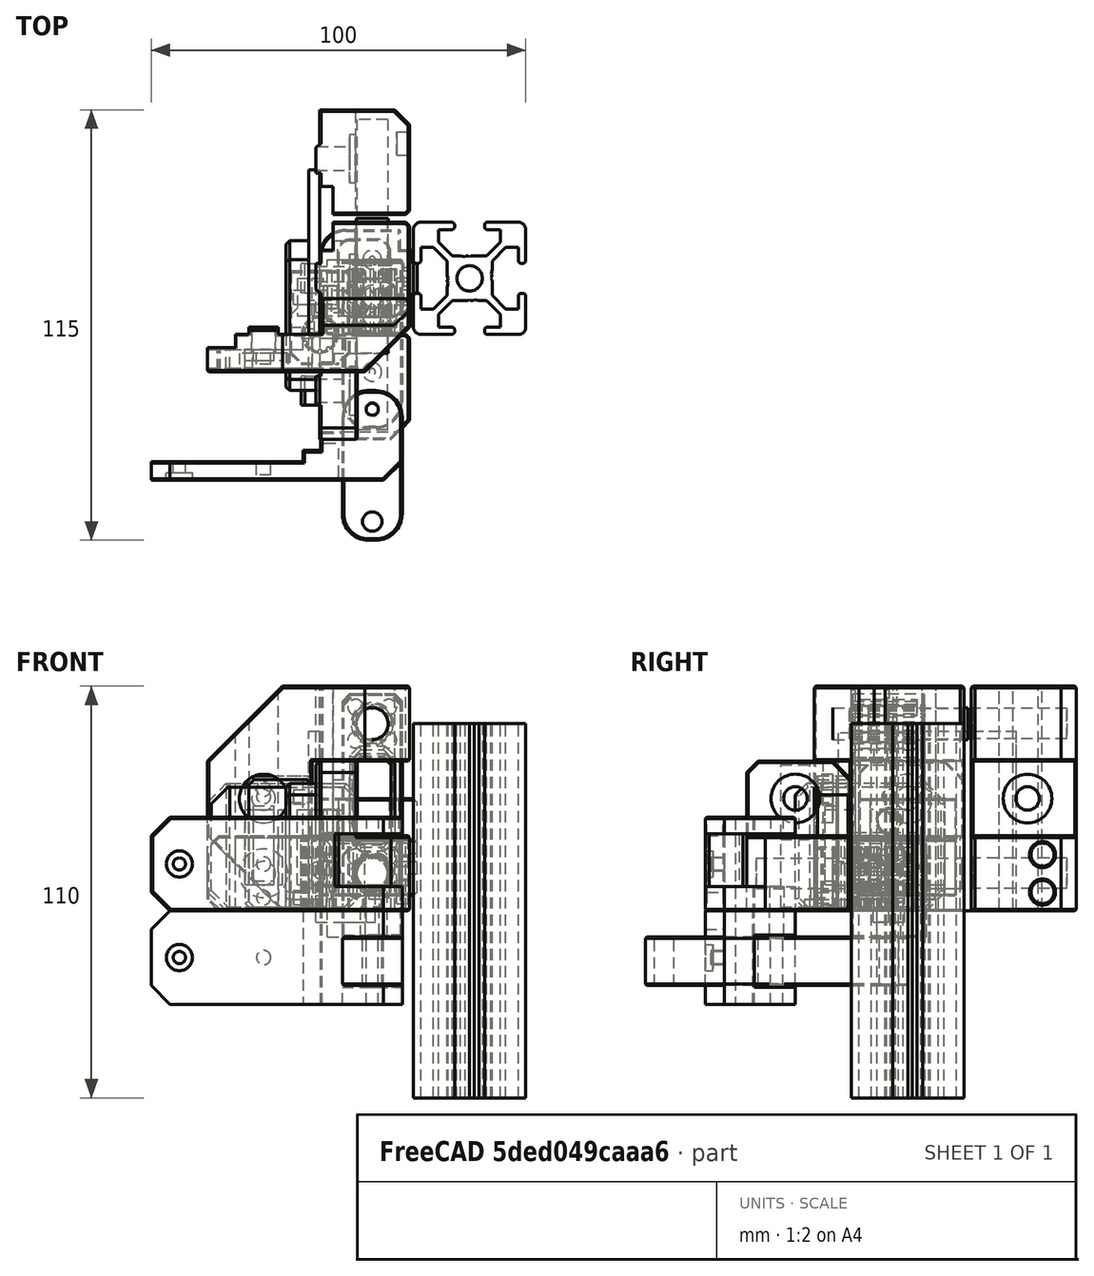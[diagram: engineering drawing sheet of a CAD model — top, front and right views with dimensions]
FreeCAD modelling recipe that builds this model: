
FCSTD DOCUMENT  (FreeCAD 0.19R24291 (Git))
Label: sliding-door
License: All rights reserved
LicenseURL: http://en.wikipedia.org/wiki/All_rights_reserved
objects: Part::Chamfer×59, Part::Box×54, Part::Cut×53, Part::Feature×52, Part::Cylinder×50, Part::MultiFuse×31, Part::Fillet×7, Part::Refine×2, App::FeaturePython×1, Part::Mirroring×1
note: 309 computed .brp shape members not serialized (recipe doc carries the construction recipe); baked Part::Feature solids carry a one-line shape summary decoded from their .brp

FEATURE [Part::Box] Box  label="Cube"
  AttacherType = Attacher::AttachEngine3D
  Height = 20
  Length = 24
  Placement = pos=(0,2,0) rot=(0,0,1;0rad)
  Width = 28
FEATURE [Part::Box] Box001  label="Cube001"
  AttacherType = Attacher::AttachEngine3D
  Height = 40
  Length = 10
  Placement = pos=(0,2,0) rot=(0,0,1;0rad)
  Width = 28
FEATURE [Part::Cylinder] Cylinder
  Angle = 360
  AttacherType = Attacher::AttachEngine3D
  Height = 36
  Placement = pos=(14,4.5,10) rot=(-1,0,0;1.5708rad)
  Radius = 4.1
FEATURE [Part::Box] Box002  label="Cube002"
  AttacherType = Attacher::AttachEngine3D
  Height = 40
  Length = 2
  Placement = pos=(-1,11.1,0) rot=(0,0,1;0rad)
  Width = 7.8
FEATURE [Part::Box] Box003  label="Cube003"
  AttacherType = Attacher::AttachEngine3D
  Height = 20
  Length = 6
  Placement = pos=(-5,11.1,0) rot=(0,0,1;0rad)
  Width = 7.8
FEATURE [Part::MultiFuse] Fusion
  Shapes = -> [Box002,Box003]
FEATURE [Part::Chamfer] Chamfer005
  Base = -> Fusion
  Edges = 3 edges r=1: [Edge17,Edge22,Edge27]
FEATURE [Part::Cylinder] Cylinder001
  Angle = 360
  AttacherType = Attacher::AttachEngine3D
  Height = 33
  Placement = pos=(8,15,30) rot=(0,1,0;1.5708rad)
  Radius = 6.5
FEATURE [Part::Cylinder] Cylinder002
  Angle = 360
  AttacherType = Attacher::AttachEngine3D
  Height = 33
  Placement = pos=(-10,15,30) rot=(0,1,0;1.5708rad)
  Radius = 3.15
FEATURE [Part::Cylinder] Cylinder003
  Angle = 360
  AttacherType = Attacher::AttachEngine3D
  Height = 10
  Placement = pos=(10,20,0) rot=(0,0,1;0rad)
  Radius = 0.85
FEATURE [Part::Cylinder] Cylinder004
  Angle = 360
  AttacherType = Attacher::AttachEngine3D
  Height = 3
  Placement = pos=(10,20,0) rot=(0,0,1;0rad)
  Radius = 2.5
FEATURE [Part::MultiFuse] Fusion003
  Placement = pos=(4,0,0) rot=(0,0,1;0rad)
  Shapes = -> [Cylinder004,Cylinder003]
FEATURE [Part::MultiFuse] Fusion005
  Shapes = -> [Cylinder001,Cylinder002]
FEATURE [Part::Box] Box004  label="Cube004"
  AttacherType = Attacher::AttachEngine3D
  Height = 25
  Length = 16
  Placement = pos=(2,0,-7) rot=(0,0,1;0rad)
  Width = 20
FEATURE [Part::Cylinder] Cylinder005
  Angle = 360
  AttacherType = Attacher::AttachEngine3D
  Height = 36
  Placement = pos=(14,-5,10) rot=(0.57735,-0.57735,-0.57735;4.18879rad)
  Radius = 4.5
FEATURE [Part::Feature] Body001  label="m5-lock-nut"
  Placement = pos=(10,10,-3) rot=(0,0,1;0rad)
  shape: bbox 9.584 x 8.3 x 7 mm, 8 faces (baked)
FEATURE [Part::Box] Box006  label="Cube006"
  AttacherType = Attacher::AttachEngine3D
  Height = 7
  Length = 10
  Placement = pos=(-1,5.85,-3) rot=(0,0,1;0rad)
  Width = 8.3
FEATURE [Part::MultiFuse] Fusion006  label="nut-cut"
  Shapes = -> [Box006,Body001]
FEATURE [Part::Chamfer] Chamfer006
  Base = -> Box004
  Edges = 2 edges r=3: [Edge2,Edge6]
FEATURE [Part::Cylinder] Cylinder006
  Angle = 360
  AttacherType = Attacher::AttachEngine3D
  Height = 8
  Placement = pos=(14,10,-7) rot=(0,0,1;0rad)
  Radius = 3.15
FEATURE [Part::Cylinder] Cylinder007
  Angle = 360
  AttacherType = Attacher::AttachEngine3D
  Height = 15
  Placement = pos=(10,10,-20) rot=(0,0,1;0rad)
  Radius = 2.6
FEATURE [Part::Cylinder] Cylinder008
  Angle = 360
  AttacherType = Attacher::AttachEngine3D
  Height = 15
  Placement = pos=(10,-20,-20) rot=(0,0,1;0rad)
  Radius = 1.6
FEATURE [Part::Box] Box007  label="Cube007"
  AttacherType = Attacher::AttachEngine3D
  Height = 13
  Length = 16
  Placement = pos=(2,-25,-20) rot=(0,0,1;0rad)
  Width = 40
FEATURE [Part::Fillet] Fillet
  Base = -> Box007
  Edges = 4 edges r=7: [Edge1,Edge3,Edge5,Edge7]
FEATURE [Part::Chamfer] Chamfer008
  Base = -> Fillet
  Edges = 16 edges r=0.4: [Edge1,Edge4,Edge5,Edge6,Edge7,Edge8,Edge9,Edge10,Edge11,Edge12,Edge14,Edge16,Edge17,Edge18,Edge19,Edge20]
FEATURE [Part::Box] Box008  label="Cube008"
  AttacherType = Attacher::AttachEngine3D
  Height = 25
  Length = 52
  Placement = pos=(-45,-39,-25) rot=(0,0,1;0rad)
  Width = 8
FEATURE [Part::Box] Box009  label="Cube009"
  AttacherType = Attacher::AttachEngine3D
  Height = 4.5
  Length = 16
  Placement = pos=(2,-39,-25) rot=(0,0,1;0rad)
  Width = 24
FEATURE [Part::Box] Box010  label="Cube010"
  AttacherType = Attacher::AttachEngine3D
  Height = 6.5
  Length = 16
  Placement = pos=(2,-39,-6.5) rot=(0,0,1;0rad)
  Width = 24
FEATURE [Part::Fillet] Fillet001
  Base = -> Box009
  Edges = 2 edges r=7: [Edge3,Edge7]
FEATURE [Part::Fillet] Fillet002
  Base = -> Box010
  Edges = 2 edges r=7: [Edge3,Edge7]
FEATURE [Part::Box] Box011  label="Cube011"
  AttacherType = Attacher::AttachEngine3D
  Height = 14
  Length = 21.75
  Placement = pos=(0.25,-39,-20.5) rot=(0,0,1;0rad)
  Width = 13
FEATURE [Part::Box] Box012  label="Cube012"
  AttacherType = Attacher::AttachEngine3D
  Height = 25
  Length = 43.5
  Placement = pos=(-48,-34,-25) rot=(0,0,1;0rad)
  Width = 8
FEATURE [Part::Chamfer] Chamfer009
  Base = -> Fillet002
  Edges = 1 edges r=5: [Edge13]
  Placement = pos=(4,0,0) rot=(0,0,1;0rad)
FEATURE [Part::Chamfer] Chamfer011
  Base = -> Fillet001
  Edges = 1 edges r=5: [Edge13]
  Placement = pos=(4,0,0) rot=(0,0,1;0rad)
FEATURE [Part::Cylinder] Cylinder010
  Angle = 360
  AttacherType = Attacher::AttachEngine3D
  Height = 18
  Placement = pos=(10,-20,-30) rot=(0,0,1;0rad)
  Radius = 1.6
FEATURE [Part::Cylinder] Cylinder011
  Angle = 360
  AttacherType = Attacher::AttachEngine3D
  Height = 18
  Placement = pos=(10,-20,-11) rot=(0,0,1;0rad)
  Radius = 1.9
FEATURE [Part::MultiFuse] Fusion010
  Placement = pos=(4,0,0) rot=(0,0,1;0rad)
  Shapes = -> [Cylinder011,Cylinder010]
FEATURE [Part::Cylinder] Cylinder012
  Angle = 360
  AttacherType = Attacher::AttachEngine3D
  Height = 10
  Placement = pos=(-15,-37.5,-12.5) rot=(-1,0,0;1.5708rad)
  Radius = 1.9
FEATURE [Part::Cylinder] Cylinder013
  Angle = 360
  AttacherType = Attacher::AttachEngine3D
  Height = 10
  Placement = pos=(-37.5,-41.5,-12.5) rot=(-1,0,0;1.5708rad)
  Radius = 1.65
FEATURE [Part::Cylinder] Cylinder014
  Angle = 360
  AttacherType = Attacher::AttachEngine3D
  Height = 2
  Placement = pos=(-37.5,-39,-12.5) rot=(-1,0,0;1.5708rad)
  Radius = 3.5
FEATURE [Part::MultiFuse] Fusion011
  Shapes = -> [Cylinder013,Cylinder012,Cylinder014]
FEATURE [Part::Feature] Common001  label="extrusion001"
  Placement = pos=(55,30,0) rot=(0,0,1;0rad)
  shape: bbox 30 x 30 x 100 mm, 95 faces (baked)
FEATURE [Part::Feature] Cylinder016001  label="Cylinder017"
  shape: bbox 1 x 1 x 20 mm, 3 faces (baked)
FEATURE [Part::Feature] Cylinder016002  label="Cylinder018"
  Placement = pos=(0,0,0) rot=(0,0,-1;0.523599rad)
  shape: bbox 1 x 1 x 20 mm, 3 faces (baked)
FEATURE [Part::Feature] Cylinder016003  label="Cylinder019"
  Placement = pos=(0,0,0) rot=(0,0,-1;1.0472rad)
  shape: bbox 1 x 1 x 20 mm, 3 faces (baked)
FEATURE [Part::Feature] Cylinder016004  label="Cylinder020"
  Placement = pos=(0,0,0) rot=(0,0,-1;1.5708rad)
  shape: bbox 1 x 1 x 20 mm, 3 faces (baked)
FEATURE [Part::Feature] Cylinder016005  label="Cylinder021"
  Placement = pos=(0,0,0) rot=(0,0,1;4.18879rad)
  shape: bbox 1 x 1 x 20 mm, 3 faces (baked)
FEATURE [Part::Feature] Cylinder016006  label="Cylinder022"
  Placement = pos=(0,0,0) rot=(0,0,1;3.66519rad)
  shape: bbox 1 x 1 x 20 mm, 3 faces (baked)
FEATURE [Part::Feature] Cylinder016007  label="Cylinder023"
  Placement = pos=(0,0,0) rot=(0,0,1;3.14159rad)
  shape: bbox 1 x 1 x 20 mm, 3 faces (baked)
FEATURE [Part::Feature] Cylinder016008  label="Cylinder024"
  Placement = pos=(0,0,0) rot=(0,0,1;2.61799rad)
  shape: bbox 1 x 1 x 20 mm, 3 faces (baked)
FEATURE [Part::Feature] Cylinder016009  label="Cylinder025"
  Placement = pos=(0,0,0) rot=(0,0,1;2.0944rad)
  shape: bbox 1 x 1 x 20 mm, 3 faces (baked)
FEATURE [Part::Feature] Cylinder016010  label="Cylinder026"
  Placement = pos=(0,0,0) rot=(0,0,1;1.5708rad)
  shape: bbox 1 x 1 x 20 mm, 3 faces (baked)
FEATURE [Part::Feature] Cylinder016011  label="Cylinder027"
  Placement = pos=(0,0,0) rot=(0,0,1;1.0472rad)
  shape: bbox 1 x 1 x 20 mm, 3 faces (baked)
FEATURE [Part::Feature] Cylinder016012  label="Cylinder028"
  Placement = pos=(0,0,0) rot=(0,0,1;0.523599rad)
  shape: bbox 1 x 1 x 20 mm, 3 faces (baked)
FEATURE [Part::MultiFuse] Fusion012
  Placement = pos=(14,2e-15,10) rot=(-1,0,0;1.5708rad)
  Shapes = -> [Cylinder016009,Cylinder016010,Cylinder016012,Cylinder016001,Cylinder016011,Cylinder016004,Cylinder016003,Cylinder016006,Cylinder016002,Cylinder016008,Cylinder016007,Cylinder016005]
FEATURE [Part::Box] Box013  label="Cube013"
  AttacherType = Attacher::AttachEngine3D
  Height = 43
  Length = 3.5
  Placement = pos=(0,22.5,0) rot=(0,0,1;0rad)
  Width = 10
FEATURE [Part::Box] Box014  label="Cube014"
  AttacherType = Attacher::AttachEngine3D
  Height = 43
  Length = 3.5
  Placement = pos=(0,22.5,0) rot=(0,0,1;0rad)
  Width = 10
FEATURE [Part::Chamfer] Chamfer
  Base = -> Box001
  Edges = 1 edges r=3: [Edge10]
FEATURE [Part::Chamfer] Chamfer016009
  Base = -> Chamfer
  Edges = 1 edges r=5: [Edge13]
FEATURE [Part::Chamfer] Chamfer016010
  Base = -> Box
  Edges = 1 edges r=5: [Edge5]
FEATURE [Part::Cut] Cut010011002
  Base = -> Chamfer016009
  Tool = -> Box013
FEATURE [Part::Chamfer] Chamfer016013
  Base = -> Cut010011002
  Edges = 13 edges r=0.4: [Edge1,Edge3,Edge4,Edge5,Edge9,Edge12,Edge13,Edge14,Edge15,Edge17,Edge19,Edge23,Edge24]
FEATURE [Part::Chamfer] Chamfer016014
  Base = -> Chamfer016010
  Edges = 1 edges r=1: [Edge3]
FEATURE [Part::Cut] Cut
  Base = -> Chamfer016014
  Tool = -> Box014
FEATURE [Part::Chamfer] Chamfer016015
  Base = -> Cut
  Edges = 16 edges r=0.4: [Edge1,Edge4,Edge5,Edge6,Edge7,Edge8,Edge9,Edge10,Edge11,Edge12,Edge14,Edge16,Edge17,Edge18,Edge19,Edge20]
FEATURE [Part::MultiFuse] Fusion016
  Shapes = -> [Chamfer016015,Chamfer016013,Chamfer005]
FEATURE [Part::Cut] Cut010011003
  Base = -> Fusion016
  Tool = -> Fusion005
FEATURE [Part::Cut] Cut010011004
  Base = -> Cut010011003
  Tool = -> Fusion003
FEATURE [Part::Cut] Cut010011005
  Base = -> Cut010011004
  Tool = -> Cylinder
FEATURE [Part::Chamfer] Chamfer016016
  Base = -> Cut010011005
  Edges = 1 edges r=0.4: [Edge24]
FEATURE [Part::Feature] Chamfer016016001  label="Chamfer016017"
  Placement = pos=(0,-30,0) rot=(0,0,1;0rad)
  shape: bbox 29 x 28 x 40 mm, 63 faces (baked)
FEATURE [Part::Cut] Cut010011006
  Base = -> Box008
  Tool = -> Box012
FEATURE [Part::Chamfer] Chamfer016016004
  Base = -> Cut010011006
  Edges = 2 edges r=5: [Edge1,Edge3]
FEATURE [Part::Box] Box015  label="Cube015"
  AttacherType = Attacher::AttachEngine3D
  Height = 25
  Length = 5.75
  Placement = pos=(0.25,-39,-25) rot=(0,0,1;0rad)
  Width = 13
FEATURE [Part::Chamfer] Chamfer016016005
  Base = -> Box011
  Edges = 1 edges r=5: [Edge5]
FEATURE [Part::Chamfer] Chamfer016016006
  Base = -> Box015
  Edges = 1 edges r=0.4: [Edge3]
FEATURE [Part::Chamfer] Chamfer016016007
  Base = -> Chamfer016016005
  Edges = 1 edges r=0.4: [Edge12]
FEATURE [Part::MultiFuse] Fusion017
  Shapes = -> [Chamfer016016007,Chamfer016016006,Chamfer011,Chamfer009,Chamfer016016004]
FEATURE [Part::Cut] Cut010011007
  Base = -> Fusion017
  Tool = -> Fusion010
FEATURE [Part::Cut] Cut010011008
  Base = -> Cut010011007
  Tool = -> Fusion011
FEATURE [Part::Feature] Cut010011008001  label="Cut010011009"
  shape: bbox 67 x 24 x 25 mm, 31 faces (baked)
FEATURE [Part::MultiFuse] Fusion009
  Shapes = -> [Cylinder008,Cylinder007]
FEATURE [Part::Cut] Cut008  label="hingle-base"
  Base = -> Chamfer008
  Placement = pos=(4,0,0) rot=(0,0,1;0rad)
  Tool = -> Fusion009
FEATURE [Part::Feature] Fusion018001  label="slider001"
  shape: bbox 16 x 25 x 20 mm, 76 faces (baked)
FEATURE [Part::Box] Box016  label="Cube016"
  AttacherType = Attacher::AttachEngine3D
  Height = 34
  Length = 25.5
  Placement = pos=(-30,-4,0) rot=(0,0,1;0rad)
  Width = 3
FEATURE [Part::Box] Box017  label="Cube017"
  AttacherType = Attacher::AttachEngine3D
  Height = 34
  Length = 40
  Placement = pos=(-30,-10,0) rot=(0,0,1;0rad)
  Width = 9
FEATURE [Part::Box] Box018  label="Cube018"
  AttacherType = Attacher::AttachEngine3D
  Height = 20
  Length = 5.5
  Placement = pos=(-17.75,-7,7) rot=(0,0,1;0rad)
  Width = 3
FEATURE [Part::Cylinder] Cylinder016013  label="Cylinder029"
  Angle = 360
  AttacherType = Attacher::AttachEngine3D
  Height = 10
  Placement = pos=(-15,1e-15,3.5) rot=(-1,0,0;1.5708rad)
  Radius = 1.9
FEATURE [Part::Cylinder] Cylinder016014  label="Cylinder030"
  Angle = 360
  AttacherType = Attacher::AttachEngine3D
  Height = 10
  Placement = pos=(-15,-6.8e-15,30.5) rot=(-1,0,0;1.5708rad)
  Radius = 1.9
FEATURE [Part::MultiFuse] Fusion018002
  Placement = pos=(0,-8,0) rot=(0,0,1;0rad)
  Shapes = -> [Cylinder016014,Cylinder016013]
FEATURE [Part::Box] Box019  label="Cube019"
  AttacherType = Attacher::AttachEngine3D
  Height = 40
  Length = 14
  Placement = pos=(-2,-10,0) rot=(0,0,1;0rad)
  Width = 9
FEATURE [Part::Cut] Cut010011008003
  Base = -> Box017
  Tool = -> Box016
FEATURE [Part::Box] Box020  label="Cube020"
  AttacherType = Attacher::AttachEngine3D
  Height = 40
  Length = 14
  Placement = pos=(-34,-10,0) rot=(0,0,1;0rad)
  Width = 9
FEATURE [Part::Feature] Chamfer016016008004001  label="door-extra-magnet001"
  shape: bbox 23 x 9 x 34 mm, 29 faces (baked)
FEATURE [Part::Box] Box021  label="Cube021"
  AttacherType = Attacher::AttachEngine3D
  Height = 20
  Length = 7.8
  Placement = pos=(-3.9,0.5,0) rot=(0,0,1;0rad)
  Width = 7.5
FEATURE [Part::Box] Box022  label="Cube022"
  AttacherType = Attacher::AttachEngine3D
  Height = 20
  Length = 16
  Placement = pos=(-8,2,0) rot=(0,0,1;0rad)
  Width = 6
FEATURE [Part::Cylinder] Cylinder016015  label="Cylinder031"
  Angle = 360
  AttacherType = Attacher::AttachEngine3D
  Height = 10
  Placement = pos=(0,0.5,4) rot=(-1,0,0;1.5708rad)
  Radius = 3.1
FEATURE [Part::Cylinder] Cylinder016016  label="Cylinder032"
  Angle = 360
  AttacherType = Attacher::AttachEngine3D
  Height = 10
  Placement = pos=(0,0.5,16) rot=(-1,0,0;1.5708rad)
  Radius = 3.1
FEATURE [Part::Cylinder] Cylinder016017  label="Cylinder033"
  Angle = 360
  AttacherType = Attacher::AttachEngine3D
  Height = 10
  Placement = pos=(0,0.5,10) rot=(-1,0,0;1.5708rad)
  Radius = 1.45
FEATURE [Part::Chamfer] Chamfer016016008004002
  Base = -> Box022
  Edges = 2 edges r=3: [Edge3,Edge7]
FEATURE [Part::MultiFuse] Fusion018004
  Placement = pos=(0,1,0) rot=(0,0,1;0rad)
  Shapes = -> [Cylinder016016,Cylinder016015]
FEATURE [Part::MultiFuse] Fusion018005
  Shapes = -> [Chamfer016016008004002,Box021]
FEATURE [Part::Cut] Cut010011008008
  Base = -> Fusion018005
  Tool = -> Fusion018004
FEATURE [Part::Cut] Cut010011008009  label="magnet-nut"
  Base = -> Cut010011008008
  Tool = -> Cylinder016017
FEATURE [Part::Cylinder] Cylinder016018  label="Cylinder034"
  Angle = 360
  AttacherType = Attacher::AttachEngine3D
  Height = 5
  Placement = pos=(-15,-10,10) rot=(-1,0,0;1.5708rad)
  Radius = 6.5
FEATURE [Part::Cylinder] Cylinder016019  label="Cylinder035"
  Angle = 360
  AttacherType = Attacher::AttachEngine3D
  Height = 21
  Placement = pos=(-15,-10,10) rot=(-1,0,0;1.5708rad)
  Radius = 3.15
FEATURE [Part::MultiFuse] Fusion018007002
  Shapes = -> [Cylinder016018,Cylinder016019]
FEATURE [Part::Feature] Cut010011008009001  label="magnet-nut001"
  shape: bbox 16 x 7.5 x 20 mm, 17 faces (baked)
FEATURE [Part::Feature] Cut010011008009003001  label="rod-mount-end001"
  shape: bbox 54 x 20 x 20 mm, 62 faces (baked)
FEATURE [Part::Box] Box023  label="Cube023"
  AttacherType = Attacher::AttachEngine3D
  Height = 48
  Length = 3
  Placement = pos=(-3,0,0) rot=(0,0,1;0rad)
  Width = 44
FEATURE [Part::Feature] Chamfer016016008003002  label="door-handle002"
  Placement = pos=(1,-5,0) rot=(0,0,-1;1.5708rad)
  shape: bbox 9 x 40 x 34 mm, 29 faces (baked)
FEATURE [Part::Box] Box024  label="Cube024"
  AttacherType = Attacher::AttachEngine3D
  Height = 20
  Length = 3
  Placement = pos=(-2,5,7) rot=(0,0,1;0rad)
  Width = 10
FEATURE [Part::Cylinder] Cylinder016020  label="Cylinder036"
  Angle = 360
  AttacherType = Attacher::AttachEngine3D
  Height = 10
  Placement = pos=(-2.2e-15,10,10) rot=(0,1,0;1.5708rad)
  Radius = 3.15
FEATURE [Part::Cylinder] Cylinder016021  label="Cylinder037"
  Angle = 360
  AttacherType = Attacher::AttachEngine3D
  Height = 10
  Placement = pos=(-5.8e-15,10,24) rot=(0,1,0;1.5708rad)
  Radius = 3.15
FEATURE [Part::Box] Box025  label="Cube025"
  AttacherType = Attacher::AttachEngine3D
  Height = 15
  Length = 25
  Placement = pos=(0,2,4) rot=(0,0,1;0rad)
  Width = 26
FEATURE [Part::Box] Box026  label="Cube026"
  AttacherType = Attacher::AttachEngine3D
  Height = 15
  Length = 2
  Placement = pos=(24,11.1,4) rot=(0,0,1;0rad)
  Width = 7.8
FEATURE [Part::Box] Box028  label="Cube028"
  AttacherType = Attacher::AttachEngine3D
  Height = 26
  Length = 2
  Placement = pos=(24,11.1,4) rot=(0,0,1;0rad)
  Width = 7.8
FEATURE [Part::Box] Box029  label="Cube029"
  AttacherType = Attacher::AttachEngine3D
  Height = 32
  Length = 17
  Placement = pos=(5,5,4) rot=(0,0,1;0rad)
  Width = 20
FEATURE [Part::Box] Box030  label="Cube030"
  AttacherType = Attacher::AttachEngine3D
  Height = 26
  Length = 25
  Placement = pos=(0,2,4) rot=(0,0,1;0rad)
  Width = 26
FEATURE [Part::MultiFuse] Fusion018007003002
  Placement = pos=(1,0,0) rot=(0,0,1;0rad)
  Shapes = -> [Cylinder016021,Cylinder016020]
FEATURE [Part::Chamfer] Chamfer016016008004009
  Base = -> Box028
  Edges = 2 edges r=1: [Edge6,Edge8]
FEATURE [Part::Cylinder] Cylinder016022  label="magnet-6x3mm001"
  Angle = 360
  AttacherType = Attacher::AttachEngine3D
  Height = 3
  Placement = pos=(2,10,10) rot=(0,1,0;1.5708rad)
  Radius = 3
FEATURE [Part::Cylinder] Cylinder016023  label="magnet-6x3mm"
  Angle = 360
  AttacherType = Attacher::AttachEngine3D
  Height = 3
  Placement = pos=(2,10,24) rot=(0,1,0;1.5708rad)
  Radius = 3
FEATURE [Part::Chamfer] Chamfer016016008004011
  Base = -> Box026
  Edges = 2 edges r=1: [Edge6,Edge8]
FEATURE [Part::Box] Box031  label="Cube031"
  AttacherType = Attacher::AttachEngine3D
  Height = 42
  Length = 10
  Placement = pos=(21.5,22.5,0) rot=(0,0,1;0rad)
  Width = 10
FEATURE [Part::Box] Box032  label="Cube032"
  AttacherType = Attacher::AttachEngine3D
  Height = 42
  Length = 10
  Placement = pos=(18.5,19.5,0) rot=(0,0,1;0rad)
  Width = 10
FEATURE [Part::Cut] Cut010011008009003005
  Base = -> Box029
  Tool = -> Box032
FEATURE [Part::Fillet] Fillet007
  Base = -> Cut010011008009003005
  Edges = 4 edges r=3: [Edge1,Edge3,Edge6,Edge13]
FEATURE [Part::Fillet] Fillet008  label="inner-cut"
  Base = -> Fillet007
  Edges = 2 edges r=1: [Edge27,Edge28]
  Placement = pos=(0,0,3) rot=(0,0,1;0rad)
FEATURE [Part::Feature] Fillet008001  label="inner-cut001"
  shape: bbox 17 x 20 x 32 mm, 14 faces (baked)
FEATURE [Part::Fillet] Fillet008002
  Base = -> Box030
  Edges = 2 edges r=7: [Edge1,Edge3]
FEATURE [Part::Cut] Cut010011008009003006
  Base = -> Fillet008002
  Tool = -> Fillet008001
FEATURE [Part::Box] Box033  label="Cube033"
  AttacherType = Attacher::AttachEngine3D
  Height = 42
  Length = 10
  Placement = pos=(21.5,22.5,0) rot=(0,0,1;0rad)
  Width = 10
FEATURE [Part::Cut] Cut010011008009003007
  Base = -> Cut010011008009003006
  Tool = -> Box033
FEATURE [Part::Chamfer] Chamfer016016008004012
  Base = -> Cut010011008009003007
  Edges = 41 edges r=0.4: [Edge1,Edge4,Edge5,Edge6,Edge7,Edge8,Edge9,Edge10,Edge11,Edge12,Edge13,Edge14,Edge15,Edge16,Edge17,Edge18,Edge19,Edge20,Edge21,Edge22,Edge23,Edge24,Edge26,Edge28,Edge29,Edge30,Edge31,Edge32,Edge33,Edge34,Edge35,Edge36,Edge37,Edge38,Edge39,Edge40,Edge41,Edge42,Edge43,Edge44,Edge45]
FEATURE [Part::Cut] Cut010011008009003008
  Base = -> Chamfer016016008004012
  Tool = -> Fusion018007003002
FEATURE [Part::Chamfer] Chamfer016016008004013
  Base = -> Cut010011008009003008
  Edges = 6 edges r=0.4: [Edge144,Edge145,Edge147,Edge148,Edge151,Edge152]
FEATURE [Part::Cut] Cut010011008009003009
  Base = -> Box025
  Tool = -> Fillet008
FEATURE [Part::Fillet] Fillet008003
  Base = -> Cut010011008009003009
  Edges = 2 edges r=7: [Edge1,Edge3]
FEATURE [Part::Cut] Cut010011008009003010
  Base = -> Fillet008003
  Tool = -> Box031
FEATURE [Part::Chamfer] Chamfer016016008004014
  Base = -> Cut010011008009003010
  Edges = 29 edges r=0.4: [Edge1,Edge4,Edge5,Edge6,Edge7,Edge8,Edge9,Edge10,Edge11,Edge12,Edge13,Edge14,Edge15,Edge16,Edge17,Edge18,Edge19,Edge20,Edge21,Edge22,Edge23,Edge24,Edge26,Edge28,Edge29,Edge30,Edge31,Edge32,Edge33]
FEATURE [Part::MultiFuse] Fusion018007003006
  Shapes = -> [Chamfer016016008004011,Chamfer016016008004014]
FEATURE [Part::Cylinder] Cylinder016024  label="Cylinder038"
  Angle = 360
  AttacherType = Attacher::AttachEngine3D
  Height = 30
  Placement = pos=(-14,15,17) rot=(0,1,0;1.5708rad)
  Radius = 2
FEATURE [Part::Cylinder] Cylinder016025  label="Cylinder039"
  Angle = 360
  AttacherType = Attacher::AttachEngine3D
  Height = 15
  Placement = pos=(-2,15,11.5) rot=(0,1,0;1.5708rad)
  Radius = 2
FEATURE [Part::Cylinder] Cylinder016026  label="Cylinder040"
  Angle = 360
  AttacherType = Attacher::AttachEngine3D
  Height = 15
  Placement = pos=(20.5,15,11.5) rot=(0,1,0;1.5708rad)
  Radius = 1.65
FEATURE [Part::Cut] Cut010011008009003011
  Base = -> Fusion018007003006
  Tool = -> Cylinder016025
FEATURE [Part::Chamfer] Chamfer016016008004015
  Base = -> Cut010011008009003011
  Edges = 1 edges r=0.4: [Edge126]
FEATURE [Part::Cylinder] Cylinder016027  label="Cylinder041"
  Angle = 360
  AttacherType = Attacher::AttachEngine3D
  Height = 3
  Placement = pos=(21,15,11.5) rot=(0,1,0;1.5708rad)
  Radius = 3
FEATURE [Part::Cut] Cut010011008009003012
  Base = -> Chamfer016016008004015
  Tool = -> Cylinder016026
FEATURE [Part::Cut] Cut010011008009003013  label="tweezer-holder-btm"
  Base = -> Cut010011008009003012
  Tool = -> Cylinder016027
FEATURE [Part::MultiFuse] Fusion018007003007
  Shapes = -> [Chamfer016016008004009,Chamfer016016008004013]
FEATURE [Part::Cylinder] Cylinder016028  label="Cylinder042"
  Angle = 360
  AttacherType = Attacher::AttachEngine3D
  Height = 3
  Placement = pos=(21,15,17) rot=(0,1,0;1.5708rad)
  Radius = 2
FEATURE [Part::Cut] Cut010011008009003014
  Base = -> Fusion018007003007
  Tool = -> Cylinder016024
FEATURE [Part::Chamfer] Chamfer016016008004016
  Base = -> Cut010011008009003014
  Edges = 1 edges r=0.4: [Edge162]
FEATURE [Part::Cylinder] Cylinder016029  label="Cylinder043"
  Angle = 360
  AttacherType = Attacher::AttachEngine3D
  Height = 30
  Placement = pos=(13,15,17) rot=(0,1,0;1.5708rad)
  Radius = 1.65
FEATURE [Part::Cut] Cut010011008009003015
  Base = -> Chamfer016016008004016
  Tool = -> Cylinder016029
FEATURE [Part::Cut] Cut010011008009003016  label="tweezer-holder-top"
  Base = -> Cut010011008009003015
  Tool = -> Cylinder016028
FEATURE [Part::Feature] Cut010011008009003016001  label="tweezer-holder-top001"
  shape: bbox 26 x 26 x 26 mm, 88 faces (baked)
FEATURE [Part::Feature] Cut010011008009003013001  label="tweezer-holder-btm001"
  shape: bbox 26 x 26 x 15 mm, 67 faces (baked)
FEATURE [Part::Cylinder] Cylinder016030  label="Cylinder044"
  Angle = 360
  AttacherType = Attacher::AttachEngine3D
  Height = 10
  Placement = pos=(20.5,12,10) rot=(0,1,0;1.5708rad)
  Radius = 3.15
FEATURE [Part::Cut] Cut010011008009003016002
  Base = -> Chamfer016016
  Tool = -> Cylinder016030
FEATURE [Part::Chamfer] Chamfer016016008004017  label="rod-mount-front-w-magnet"
  Base = -> Cut010011008009003016002
  Edges = 1 edges r=0.4: [Edge48]
FEATURE [Part::Feature] Chamfer016016008004017001  label="rod-mount-front-w-magnet001"
  shape: bbox 29 x 28 x 40 mm, 66 faces (baked)
FEATURE [Part::Box] Box034  label="Cube034"
  AttacherType = Attacher::AttachEngine3D
  Height = 20
  Length = 5.5
  Placement = pos=(-17.75,-7,8) rot=(0,0,1;0rad)
  Width = 3
FEATURE [Part::Cylinder] Cylinder016032  label="Cylinder046"
  Angle = 360
  AttacherType = Attacher::AttachEngine3D
  Height = 10
  Placement = pos=(-15,-7.2e-15,32.5) rot=(-1,0,0;1.5708rad)
  Radius = 1.9
FEATURE [Part::Box] Box035  label="Cube035"
  AttacherType = Attacher::AttachEngine3D
  Height = 36
  Length = 40
  Placement = pos=(-30,-10,0) rot=(0,0,1;0rad)
  Width = 9
FEATURE [Part::Cylinder] Cylinder016033  label="Cylinder047"
  Angle = 360
  AttacherType = Attacher::AttachEngine3D
  Height = 10
  Placement = pos=(-15,1e-15,3.5) rot=(-1,0,0;1.5708rad)
  Radius = 1.9
FEATURE [Part::Box] Box036  label="Cube036"
  AttacherType = Attacher::AttachEngine3D
  Height = 36
  Length = 25.5
  Placement = pos=(-30,-4,0) rot=(0,0,1;0rad)
  Width = 3
FEATURE [Part::Cut] Cut010011008009003016003
  Base = -> Box035
  Tool = -> Box036
FEATURE [Part::Cut] Cut010011008009003016004
  Base = -> Cut010011008009003016003
  Tool = -> Box019
FEATURE [Part::MultiFuse] Fusion018007003008
  Placement = pos=(0,-8,0) rot=(0,0,1;0rad)
  Shapes = -> [Cylinder016032,Cylinder016033]
FEATURE [Part::Box] Box037  label="Cube037"
  AttacherType = Attacher::AttachEngine3D
  Height = 60
  Length = 3.5
  Placement = pos=(0,22.5,0) rot=(0,0,1;0rad)
  Width = 10
FEATURE [Part::Cylinder] Cylinder016034
  Angle = 360
  AttacherType = Attacher::AttachEngine3D
  Height = 33
  Placement = pos=(8,15,30) rot=(0,1,0;1.5708rad)
  Radius = 6.5
FEATURE [Part::Box] Box040  label="Cube040"
  AttacherType = Attacher::AttachEngine3D
  Height = 60
  Length = 9.5
  Placement = pos=(0,2,0) rot=(0,0,1;0rad)
  Width = 28
FEATURE [Part::Cylinder] Cylinder016035
  Angle = 360
  AttacherType = Attacher::AttachEngine3D
  Height = 10
  Placement = pos=(20.5,12,5) rot=(0,1,0;1.5708rad)
  Radius = 3.1
FEATURE [Part::Box] Box041  label="Cube041"
  AttacherType = Attacher::AttachEngine3D
  Height = 60
  Length = 2
  Placement = pos=(-1,11.1,0) rot=(0,0,1;0rad)
  Width = 7.8
FEATURE [Part::Cylinder] Cylinder016036
  Angle = 360
  AttacherType = Attacher::AttachEngine3D
  Height = 36
  Placement = pos=(14,4.5,10) rot=(-1,0,0;1.5708rad)
  Radius = 4.1
FEATURE [Part::Box] Box042  label="Cube042"
  AttacherType = Attacher::AttachEngine3D
  Height = 20
  Length = 24
  Placement = pos=(0,2,0) rot=(0,0,1;0rad)
  Width = 28
FEATURE [Part::Cylinder] Cylinder016039
  Angle = 360
  AttacherType = Attacher::AttachEngine3D
  Height = 33
  Placement = pos=(-10,15,30) rot=(0,1,0;1.5708rad)
  Radius = 3.15
FEATURE [Part::MultiFuse] Fusion018007003011
  Shapes = -> [Cylinder016034,Cylinder016039]
FEATURE [Part::Cylinder] Cylinder016040
  Angle = 360
  AttacherType = Attacher::AttachEngine3D
  Height = 10
  Placement = pos=(20.5,12,15) rot=(0,1,0;1.5708rad)
  Radius = 3.1
FEATURE [Part::Cut] Cut010011008009003016015
  Base = -> Cut010011008003
  Tool = -> Box018
FEATURE [Part::Cut] Cut010011008009003016016
  Base = -> Cut010011008009003016015
  Tool = -> Fusion018002
FEATURE [Part::Chamfer] Chamfer016016008004017002011
  Base = -> Cut010011008009003016016
  Edges = 2 edges r=5: [Edge1,Edge3]
FEATURE [Part::Chamfer] Chamfer016016008004017002012
  Base = -> Chamfer016016008004017002011
  Edges = 2 edges r=3: [Edge23,Edge28]
FEATURE [Part::Chamfer] Chamfer016016008004017002013  label="door-hanlde-sm-mag"
  Base = -> Chamfer016016008004017002012
  Edges = 8 edges r=1: [Edge1,Edge2,Edge3,Edge4,Edge5,Edge6,Edge7,Edge8]
FEATURE [Part::Chamfer] Chamfer016016008004017002014
  Base = -> Box042
  Edges = 1 edges r=4: [Edge5]
FEATURE [Part::Chamfer] Chamfer016016008004017002015
  Base = -> Chamfer016016008004017002014
  Edges = 1 edges r=1: [Edge4]
FEATURE [Part::Chamfer] Chamfer016016008004017002016
  Base = -> Chamfer016016008004017002015
  Edges = 12 edges r=0.4: [Edge1,Edge3,Edge5,Edge6,Edge7,Edge8,Edge9,Edge10,Edge12,Edge14,Edge15,Edge16]
FEATURE [Part::Feature] Chamfer016016008004017002013001  label="door-hanlde-sm-mag001"
  shape: bbox 40 x 9 x 34 mm, 29 faces (baked)
FEATURE [Part::Cut] Cut010011008009003016022
  Base = -> Cut010011008009003016004
  Tool = -> Box020
FEATURE [Part::Chamfer] Chamfer016016008004017002013003
  Base = -> Cut010011008009003016022
  Edges = 2 edges r=2: [Edge1,Edge9]
FEATURE [Part::Chamfer] Chamfer016016008004017002013004
  Base = -> Chamfer016016008004017002013003
  Edges = 2 edges r=1: [Edge4,Edge22]
FEATURE [Part::Cut] Cut010011008009003016023
  Base = -> Chamfer016016008004017002013004
  Tool = -> Fusion018007003008
FEATURE [Part::Cut] Cut010011008009003016024
  Base = -> Cut010011008009003016023
  Tool = -> Box034
FEATURE [Part::Chamfer] Chamfer016016008004017002013005  label="dock-magnet-mounter"
  Base = -> Cut010011008009003016024
  Edges = 8 edges r=1: [Edge1,Edge7,Edge8,Edge9,Edge10,Edge11,Edge12,Edge13]
FEATURE [Part::Feature] Chamfer016016008004017002013005001  label="dock-magnet-mounter001"
  shape: bbox 18 x 9 x 36 mm, 29 faces (baked)
FEATURE [App::FeaturePython] Dimension  label="Distance"  # Draft dimension (typed FeaturePython)
  Diameter = false
  Dimline = (21.5,4.5,19.6)
  Direction = (0,0,0)
  Distance = 7.07107
  End = (19,2,19.6)
  Normal = (0,0,1)
  Start = (24,7,19.6)
FEATURE [Part::MultiFuse] Fusion018007003013002002
  Placement = pos=(0,-1,0) rot=(0,0,1;0rad)
  Shapes = -> [Cylinder016035,Cylinder016040]
FEATURE [Part::Box] Box043  label="Cube043"
  AttacherType = Attacher::AttachEngine3D
  Height = 14
  Length = 23
  Placement = pos=(0,-29,-20.5) rot=(0,0,1;0rad)
  Width = 10
FEATURE [Part::Feature] Cut008001001001  label="hingle-base003"
  Placement = pos=(14,-20,0) rot=(0,0,1;3.14159rad)
  shape: bbox 16 x 40 x 13 mm, 28 faces (baked)
FEATURE [Part::Cut] Cut010011008009003016026002
  Base = -> Cut010011008
  Tool = -> Box043
FEATURE [Part::Chamfer] Chamfer016016008004017002013005003
  Base = -> Cut010011008009003016026002
  Edges = 2 edges r=1: [Edge44,Edge46]
FEATURE [Part::Box] Box044  label="Cube044"
  AttacherType = Attacher::AttachEngine3D
  Height = 14
  Length = 19
  Placement = pos=(5,-40.5,-20.5) rot=(0,0,1;0rad)
  Width = 29
FEATURE [Part::Cut] Cut010011008009003016026003
  Base = -> Chamfer016016008004017002013005003
  Tool = -> Box044
FEATURE [Part::Chamfer] Chamfer016016008004017002013005004
  Base = -> Cut010011008009003016026003
  Edges = 1 edges r=1: [Edge60]
FEATURE [Part::Refine] Chamfer016016008004017002013005004001
  Source = -> Chamfer016016008004017002013005004
FEATURE [Part::Chamfer] Chamfer016016008004017002013005004002
  Base = -> Chamfer016016008004017002013005004001
  Edges = 32 edges r=0.4: [Edge27,Edge30,Edge33,Edge34,Edge36,Edge39,Edge41,Edge43,Edge48,Edge49,Edge50,Edge51,Edge52,Edge56,Edge59,Edge61,Edge66,Edge68,Edge70,Edge75,Edge77,Edge83,Edge85,Edge87,Edge88,Edge91,Edge93,Edge95,Edge97,Edge98,Edge108,Edge109]
FEATURE [Part::Mirroring] Part__Mirroring002  label="Chamfer016016008004017002013005004002 (Mirror #2)"
  Base = (0,0,0)
  Normal = (0,0,1)
  Source = -> Chamfer016016008004017002013005004002
FEATURE [Part::Feature] Part__Mirroring002001  label="Chamfer016016008004017002013005004002 (Mirror #2)001"
  shape: bbox 67 x 24 x 25 mm, 71 faces (baked)
FEATURE [Part::Feature] Chamfer016016008004017002016001
  Placement = pos=(0,0,40) rot=(0,0,1;0rad)
  shape: bbox 24 x 28 x 20 mm, 20 faces (baked)
FEATURE [Part::Cylinder] Cylinder016041
  Angle = 360
  AttacherType = Attacher::AttachEngine3D
  Height = 36
  Placement = pos=(14,4.5,50) rot=(-1,0,0;1.5708rad)
  Radius = 4.1
FEATURE [Part::Chamfer] Chamfer016016008004017002013005004003
  Base = -> Box041
  Edges = 1 edges r=1: [Edge1]
FEATURE [Part::Cut] Cut010011008009003016026004
  Base = -> Chamfer016016008004017002016
  Tool = -> Fusion018007003013002002
FEATURE [Part::Chamfer] Chamfer016016008004017002013005004005
  Base = -> Cut010011008009003016026004
  Edges = 2 edges r=0.4: [Edge5,Edge6]
FEATURE [Part::Cut] Cut010011008009003016026005
  Base = -> Chamfer016016008004017002013005004005
  Tool = -> Cylinder016036
FEATURE [Part::Cut] Cut010011008009003016026006
  Base = -> Chamfer016016008004017002016001
  Tool = -> Cylinder016041
FEATURE [Part::Chamfer] Chamfer016016008004017002013005004006
  Base = -> Cut010011008009003016026005
  Edges = 1 edges r=0.4: [Edge42]
FEATURE [Part::Chamfer] Chamfer016016008004017002013005004007
  Base = -> Cut010011008009003016026006
  Edges = 1 edges r=0.4: [Edge34]
FEATURE [Part::Chamfer] Chamfer016016008004017002013005004008
  Base = -> Box040
  Edges = 12 edges r=0.4: [Edge1,Edge2,Edge3,Edge4,Edge5,Edge6,Edge7,Edge8,Edge9,Edge10,Edge11,Edge12]
FEATURE [Part::MultiFuse] Fusion018007003013002003
  Shapes = -> [Chamfer016016008004017002013005004006,Chamfer016016008004017002013005004008,Chamfer016016008004017002013005004007]
FEATURE [Part::Cut] Cut010011008009003016026007
  Base = -> Fusion018007003013002003
  Tool = -> Box037
FEATURE [Part::MultiFuse] Fusion018007003013002004
  Shapes = -> [Cut010011008009003016026007,Chamfer016016008004017002013005004003]
FEATURE [Part::Cut] Cut010011008009003016026008
  Base = -> Fusion018007003013002004
  Tool = -> Fusion018007003011
FEATURE [Part::Feature] Part__Mirroring002002  label="front-rod-mount-dual"
  Placement = pos=(8e-15,62,0) rot=(0,0,1;3.14159rad)
  shape: bbox 25 x 28 x 60 mm, 68 faces (baked)
FEATURE [Part::Feature] Fusion018007003001  label="Fusion018007004"
  shape: bbox 54 x 20 x 20 mm, 16 faces (baked)
FEATURE [Part::Chamfer] Chamfer016016008004003
  Base = -> Fusion018007003001
  Edges = 2 edges r=3: [Edge15,Edge27]
FEATURE [Part::Chamfer] Chamfer016016008004004
  Base = -> Chamfer016016008004003
  Edges = 1 edges r=12: [Edge14]
FEATURE [Part::Chamfer] Chamfer016016008004005
  Base = -> Chamfer016016008004004
  Edges = 1 edges r=1: [Edge23]
FEATURE [Part::Chamfer] Chamfer016016008004006
  Base = -> Chamfer016016008004005
  Edges = 33 edges r=0.4: [Edge1,Edge2,Edge3,Edge4,Edge5,Edge6,Edge7,Edge8,Edge9,Edge10,Edge11,Edge12,Edge13,Edge14,Edge17,Edge19,Edge21,Edge23,Edge25,Edge26,Edge27,Edge28,Edge30,Edge32,Edge33,Edge36,Edge37,Edge38,Edge39,Edge41,Edge43,Edge46,Edge47]
FEATURE [Part::Cut] Cut010011008009002
  Base = -> Chamfer016016008004006
  Tool = -> Fusion018007002
FEATURE [Part::Chamfer] Chamfer016016008004007
  Base = -> Cut010011008009002
  Edges = 1 edges r=0.4: [Edge61]
FEATURE [Part::Feature] Chamfer016016008004007001
  shape: bbox 54 x 20 x 20 mm, 59 faces (baked)
FEATURE [Part::Box] Box045  label="Cube045"
  AttacherType = Attacher::AttachEngine3D
  Height = 22
  Length = 10
  Placement = pos=(-20,1,0) rot=(0,0,1;0rad)
  Width = 10
FEATURE [Part::Cut] Cut010011008009003016026009  label="back-rod-mount"
  Base = -> Chamfer016016008004007001
  Tool = -> Box045
FEATURE [Part::Feature] Fusion018007003013002005  label="slider002"
  Placement = pos=(14,2e-15,10) rot=(-1,0,0;1.5708rad)
  shape: bbox 16 x 20 x 25 mm, 148 faces (baked)
FEATURE [Part::Cylinder] Cylinder016042
  Angle = 360
  AttacherType = Attacher::AttachEngine3D
  Height = 36
  Placement = pos=(14,-5,50) rot=(0.57735,-0.57735,-0.57735;4.18879rad)
  Radius = 4.5
FEATURE [Part::Feature] Fusion012001
  Placement = pos=(14,1.1e-14,50) rot=(-1,0,0;1.5708rad)
  shape: bbox 10 x 20 x 10 mm, 36 faces, 12 solids (baked)
FEATURE [Part::Box] Box046  label="Cube046"
  AttacherType = Attacher::AttachEngine3D
  Height = 65
  Length = 16
  Placement = pos=(6,0,-7) rot=(0,0,1;0rad)
  Width = 19.5
FEATURE [Part::Chamfer] Chamfer016016008004017002013005004009
  Base = -> Box046
  Edges = 2 edges r=3: [Edge2,Edge6]
FEATURE [Part::Chamfer] Chamfer016016008004017002013005004010
  Base = -> Chamfer016016008004017002013005004009
  Edges = 14 edges r=0.4: [Edge1,Edge2,Edge3,Edge5,Edge6,Edge7,Edge8,Edge9,Edge10,Edge12,Edge13,Edge14,Edge15,Edge16]
FEATURE [Part::MultiFuse] Fusion018007003013002006
  Shapes = -> [Cylinder005,Cylinder016042]
FEATURE [Part::Cut] Cut010011008009003016026010
  Base = -> Chamfer016016008004017002013005004010
  Tool = -> Fusion018007003013002006
FEATURE [Part::MultiFuse] Fusion018007003013002007
  Shapes = -> [Fusion012001,Fusion012]
FEATURE [Part::Box] Box047  label="Cube047"
  AttacherType = Attacher::AttachEngine3D
  Height = 60
  Length = 11
  Placement = pos=(8.5,19.5,0) rot=(0,0,1;0rad)
  Width = 4
FEATURE [Part::Box] Box048  label="Cube048"
  AttacherType = Attacher::AttachEngine3D
  Height = 26
  Length = 10
  Placement = pos=(9,-2,17) rot=(0,0,1;0rad)
  Width = 25
FEATURE [Part::Chamfer] Chamfer016016008004017002013005004011
  Base = -> Box048
  Edges = 4 edges r=2: [Edge2,Edge4,Edge6,Edge8]
FEATURE [Part::Cut] Cut010011008009003016026011
  Base = -> Fusion018007003013002007
  Tool = -> Box047
FEATURE [Part::Cut] Cut010011008009003016026012
  Base = -> Cut010011008009003016026010
  Tool = -> Chamfer016016008004017002013005004011
FEATURE [Part::MultiFuse] Fusion018007003013002008
  Shapes = -> [Cut010011008009003016026011,Cut010011008009003016026012]
FEATURE [Part::Chamfer] Chamfer016016008004017002013005004012  label="dual-slider"
  Base = -> Fusion018007003013002008
  Edges = 8 edges r=1: [Edge153,Edge155,Edge157,Edge159,Edge162,Edge163,Edge165,Edge167]
FEATURE [Part::Cut] Cut010011008009003016026013
  Base = -> Chamfer016016008004017002013005004012
  Tool = -> Cylinder006
FEATURE [Part::Box] Box049  label="Cube049"
  AttacherType = Attacher::AttachEngine3D
  Height = 59
  Length = 28
  Placement = pos=(-30,-10,0.5) rot=(0,0,1;0rad)
  Width = 6.5
FEATURE [Part::Box] Box050  label="Cube050"
  AttacherType = Attacher::AttachEngine3D
  Height = 59
  Length = 20.5
  Placement = pos=(-22.5,-3.5,0.5) rot=(0,0,1;0rad)
  Width = 3.5
FEATURE [Part::Box] Box051  label="Cube051"
  AttacherType = Attacher::AttachEngine3D
  Height = 59
  Length = 7.8
  Placement = pos=(-18.9,-2.5,0.5) rot=(0,0,1;0rad)
  Width = 3.5
FEATURE [Part::Feature] Defeatured001
  shape: bbox 54 x 20 x 20 mm, 22 faces (baked)
FEATURE [Part::Feature] Defeatured001001
  Placement = pos=(0,0,40) rot=(0,0,1;0rad)
  shape: bbox 54 x 20 x 20 mm, 22 faces (baked)
FEATURE [Part::MultiFuse] Fusion018007003013002009
  Shapes = -> [Defeatured001001,Box049,Box050,Box051,Defeatured001]
FEATURE [Part::Box] Box053  label="Cube053"
  AttacherType = Attacher::AttachEngine3D
  Height = 21
  Length = 21
  Placement = pos=(-31,-10,40) rot=(0,0,1;0rad)
  Width = 11
FEATURE [Part::Box] Box054  label="Cube054"
  AttacherType = Attacher::AttachEngine3D
  Height = 21
  Length = 21
  Placement = pos=(-31,-10,-1) rot=(0,0,1;0rad)
  Width = 11
FEATURE [Part::Chamfer] Chamfer016016008004017002013005004013
  Base = -> Box054
  Edges = 1 edges r=20: [Edge6]
FEATURE [Part::Cut] Cut010011008009003016026014
  Base = -> Fusion018007003013002009
  Tool = -> Chamfer016016008004017002013005004013
FEATURE [Part::Chamfer] Chamfer016016008004017002013005004014
  Base = -> Box053
  Edges = 1 edges r=20: [Edge8]
FEATURE [Part::Cut] Cut010011008009003016026015
  Base = -> Cut010011008009003016026014
  Tool = -> Chamfer016016008004017002013005004014
FEATURE [Part::Cylinder] Cylinder016043
  Angle = 360
  AttacherType = Attacher::AttachEngine3D
  Height = 18
  Placement = pos=(-15,-5,10) rot=(1,0,0;1.5708rad)
  Radius = 6.5
FEATURE [Part::Cylinder] Cylinder016044
  Angle = 360
  AttacherType = Attacher::AttachEngine3D
  Height = 18
  Placement = pos=(-15,4,10) rot=(1,0,0;1.5708rad)
  Radius = 3.15
FEATURE [Part::MultiFuse] Fusion018007003013002010
  Placement = pos=(0,0,20) rot=(0,0,1;0rad)
  Shapes = -> [Cylinder016044,Cylinder016043]
FEATURE [Part::Cut] Cut010011008009003016026016
  Base = -> Cut010011008009003016026015
  Tool = -> Fusion018007003013002010
FEATURE [Part::Box] Box055  label="Cube055"
  AttacherType = Attacher::AttachEngine3D
  Height = 60
  Length = 10
  Placement = pos=(-9.5,0,0) rot=(0,0,1;0rad)
  Width = 10
FEATURE [Part::Cut] Cut010011008009003016026017
  Base = -> Cut010011008009003016026016
  Tool = -> Box055
FEATURE [Part::Refine] Cut010011008009003016026017001
  Source = -> Cut010011008009003016026017
FEATURE [Part::Chamfer] Chamfer016016008004017002013005004015
  Base = -> Cut010011008009003016026017001
  Edges = 33 edges r=0.4: [Edge1,Edge2,Edge3,Edge4,Edge5,Edge6,Edge7,Edge10,Edge12,Edge16,Edge25,Edge35,Edge36,Edge37,Edge38,Edge39,Edge40,Edge42,Edge43,Edge44,Edge45,Edge46,Edge48,Edge50,Edge52,Edge53,Edge54,Edge55,Edge56,Edge58,Edge64,Edge75,Edge83]
FEATURE [Part::Feature] Chamfer016016008004017002013005004015001
  shape: bbox 54 x 20 x 60 mm, 72 faces (baked)
FEATURE [Part::Cylinder] Cylinder016045
  Angle = 360
  AttacherType = Attacher::AttachEngine3D
  Height = 36
  Placement = pos=(14,-5,10) rot=(0.57735,-0.57735,-0.57735;4.18879rad)
  Radius = 5.25
FEATURE [Part::Cylinder] Cylinder016046
  Angle = 360
  AttacherType = Attacher::AttachEngine3D
  Height = 8
  Placement = pos=(14,10,-7) rot=(0,0,1;0rad)
  Radius = 3.15
FEATURE [Part::Feature] Cylinder016047
  shape: bbox 1 x 1 x 20 mm, 3 faces (baked)
FEATURE [Part::Feature] Cylinder016048
  Placement = pos=(0,0,0) rot=(0,0,-1;0.523599rad)
  shape: bbox 1 x 1 x 20 mm, 3 faces (baked)
FEATURE [Part::Feature] Cylinder016049
  Placement = pos=(0,0,0) rot=(0,0,-1;1.0472rad)
  shape: bbox 1 x 1 x 20 mm, 3 faces (baked)
FEATURE [Part::Feature] Cylinder016050
  Placement = pos=(0,0,0) rot=(0,0,-1;1.5708rad)
  shape: bbox 1 x 1 x 20 mm, 3 faces (baked)
FEATURE [Part::Feature] Cylinder016051
  Placement = pos=(0,0,0) rot=(0,0,1;4.18879rad)
  shape: bbox 1 x 1 x 20 mm, 3 faces (baked)
FEATURE [Part::Feature] Cylinder016052
  Placement = pos=(0,0,0) rot=(0,0,1;3.66519rad)
  shape: bbox 1 x 1 x 20 mm, 3 faces (baked)
FEATURE [Part::Feature] Cylinder016053
  Placement = pos=(0,0,0) rot=(0,0,1;3.14159rad)
  shape: bbox 1 x 1 x 20 mm, 3 faces (baked)
FEATURE [Part::Feature] Cylinder016054
  Placement = pos=(0,0,0) rot=(0,0,1;2.61799rad)
  shape: bbox 1 x 1 x 20 mm, 3 faces (baked)
FEATURE [Part::Feature] Cylinder016055
  Placement = pos=(0,0,0) rot=(0,0,1;2.0944rad)
  shape: bbox 1 x 1 x 20 mm, 3 faces (baked)
FEATURE [Part::Feature] Cylinder016056
  Placement = pos=(0,0,0) rot=(0,0,1;1.5708rad)
  shape: bbox 1 x 1 x 20 mm, 3 faces (baked)
FEATURE [Part::Feature] Cylinder016057
  Placement = pos=(0,0,0) rot=(0,0,1;1.0472rad)
  shape: bbox 1 x 1 x 20 mm, 3 faces (baked)
FEATURE [Part::Feature] Cylinder016058
  Placement = pos=(0,0,0) rot=(0,0,1;0.523599rad)
  shape: bbox 1 x 1 x 20 mm, 3 faces (baked)
FEATURE [Part::MultiFuse] Fusion018007003013002011
  Placement = pos=(14,2e-15,10) rot=(-1,0,0;1.5708rad)
  Shapes = -> [Cylinder016055,Cylinder016056,Cylinder016058,Cylinder016047,Cylinder016057,Cylinder016050,Cylinder016049,Cylinder016052,Cylinder016048,Cylinder016054,Cylinder016053,Cylinder016051]
FEATURE [Part::Cylinder] Cylinder016059
  Angle = 360
  AttacherType = Attacher::AttachEngine3D
  Height = 36
  Placement = pos=(14,-5,50) rot=(0.57735,-0.57735,-0.57735;4.18879rad)
  Radius = 4.25
FEATURE [Part::Feature] Fusion018007003013002012
  Placement = pos=(14,1.1e-14,50) rot=(-1,0,0;1.5708rad)
  shape: bbox 10 x 20 x 10 mm, 36 faces, 12 solids (baked)
FEATURE [Part::Box] Box056  label="Cube056"
  AttacherType = Attacher::AttachEngine3D
  Height = 65
  Length = 16
  Placement = pos=(6,0,-7) rot=(0,0,1;0rad)
  Width = 19.5
FEATURE [Part::MultiFuse] Fusion018007003013002014
  Shapes = -> [Fusion018007003013002012,Fusion018007003013002011]
FEATURE [Part::Box] Box057  label="Cube057"
  AttacherType = Attacher::AttachEngine3D
  Height = 60
  Length = 11
  Placement = pos=(8.5,19.5,0) rot=(0,0,1;0rad)
  Width = 4
FEATURE [Part::Box] Box058  label="Cube058"
  AttacherType = Attacher::AttachEngine3D
  Height = 22
  Length = 10
  Placement = pos=(9,-2,19) rot=(0,0,1;0rad)
  Width = 25
FEATURE [Part::Cut] Cut010011008009003016026017003
  Base = -> Fusion018007003013002014
  Tool = -> Box057
FEATURE [Part::Cylinder] Cylinder016060
  Angle = 360
  AttacherType = Attacher::AttachEngine3D
  Height = 15.5
  Placement = pos=(18.4194,2,14.4194) rot=(-0.862856,-0.357407,-0.357407;1.71777rad)
  Radius = 2.1
FEATURE [Part::Cylinder] Cylinder016061
  Angle = 360
  AttacherType = Attacher::AttachEngine3D
  Height = 15.5
  Placement = pos=(9.58058,2,5.58058) rot=(-0.862856,-0.357407,-0.357407;1.71777rad)
  Radius = 2.1
FEATURE [Part::Cylinder] Cylinder016062
  Angle = 360
  AttacherType = Attacher::AttachEngine3D
  Height = 15.5
  Placement = pos=(18.4194,2,5.58058) rot=(-0.862856,-0.357407,-0.357407;1.71777rad)
  Radius = 2.1
FEATURE [Part::Cylinder] Cylinder016063
  Angle = 360
  AttacherType = Attacher::AttachEngine3D
  Height = 15.5
  Placement = pos=(9.58058,2,14.4194) rot=(-0.862856,-0.357407,-0.357407;1.71777rad)
  Radius = 2.1
FEATURE [Part::Chamfer] Chamfer016016008004017002013005004015006
  Base = -> Box058
  Edges = 4 edges r=2: [Edge2,Edge4,Edge6,Edge8]
FEATURE [Part::Chamfer] Chamfer016016008004017002013005004015007
  Base = -> Box056
  Edges = 2 edges r=2: [Edge2,Edge6]
FEATURE [Part::Cut] Cut010011008009003016026017004
  Base = -> Chamfer016016008004017002013005004015007
  Tool = -> Chamfer016016008004017002013005004015006
FEATURE [Part::Cut] Cut010011008009003016026017005
  Base = -> Cut010011008009003016026017004
  Tool = -> Cylinder016046
FEATURE [Part::MultiFuse] Fusion018007003013002015
  Shapes = -> [Cylinder016045,Cylinder016060,Cylinder016061,Cylinder016062,Cylinder016063]
FEATURE [Part::Feature] Fusion018007003013002015001
  Placement = pos=(0,0,40) rot=(0,0,1;0rad)
  shape: bbox 13.04 x 36 x 13.04 mm, 18 faces (baked)
FEATURE [Part::MultiFuse] Fusion018007003013002015002
  Shapes = -> [Fusion018007003013002015001,Fusion018007003013002015]
FEATURE [Part::Cut] Cut010011008009003016026017006
  Base = -> Cut010011008009003016026017005
  Tool = -> Fusion018007003013002015002
FEATURE [Part::Chamfer] Chamfer016016008004017002013005004015008
  Base = -> Cut010011008009003016026017006
  Edges = 26 edges r=0.4: [Edge1,Edge2,Edge3,Edge5,Edge6,Edge7,Edge8,Edge9,Edge10,Edge19,Edge20,Edge21,Edge23,Edge24,Edge25,Edge26,Edge27,Edge28,Edge29,Edge30,Edge31,Edge32,Edge33,Edge34,Edge35,Edge36]
FEATURE [Part::Chamfer] Chamfer016016008004017002013005004015009
  Base = -> Chamfer016016008004017002013005004015008
  Edges = 8 edges r=1: [Edge29,Edge30,Edge31,Edge32,Edge33,Edge34,Edge35,Edge36]
FEATURE [Part::Chamfer] Chamfer016016008004017002013005004015010
  Base = -> Chamfer016016008004017002013005004015009
  Edges = 16 edges r=0.2: [Edge86,Edge88,Edge90,Edge92,Edge94,Edge96,Edge98,Edge100,Edge104,Edge106,Edge108,Edge110,Edge112,Edge114,Edge116,Edge118]
